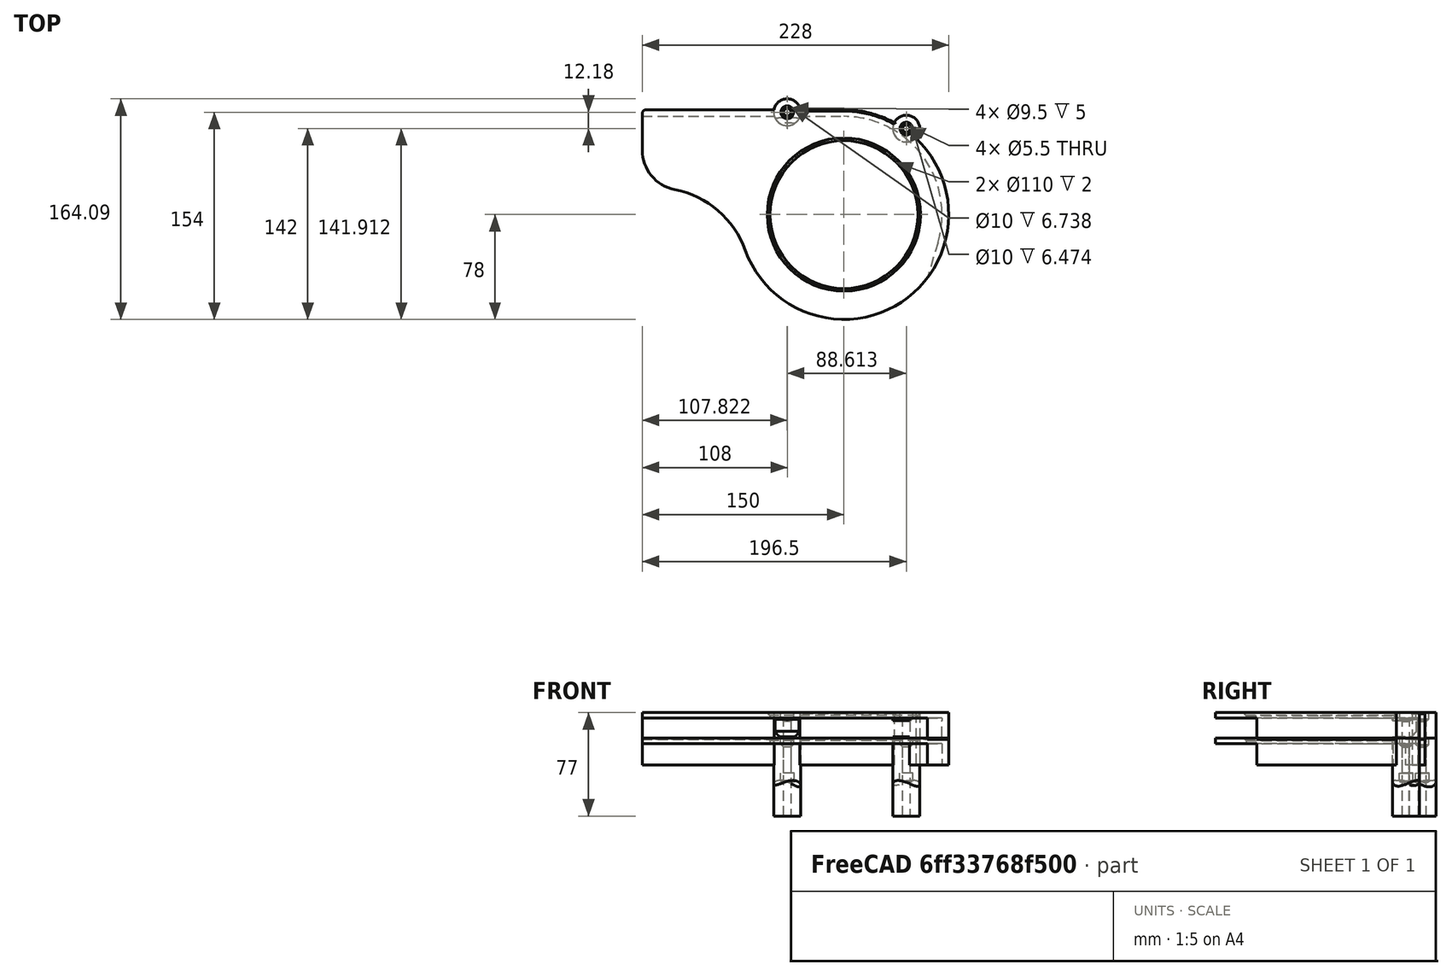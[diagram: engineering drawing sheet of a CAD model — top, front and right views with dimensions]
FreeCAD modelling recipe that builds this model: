
FCSTD DOCUMENT  (FreeCAD 0.19R)
Label: R3
License: All rights reserved
LicenseURL: http://en.wikipedia.org/wiki/All_rights_reserved
objects: Part::Cylinder×6, Sketcher::SketchObject×5, Part::Cut×4, PartDesign::Pocket×3, PartDesign::Chamfer×3, PartDesign::Pad×2, Part::MultiFuse×2, PartDesign::Fillet×1, PartDesign::Body×1, Part::Chamfer×1
note: 37 computed .brp shape members not serialized (recipe doc carries the construction recipe); baked Part::Feature solids carry a one-line shape summary decoded from their .brp

FEATURE [Sketcher::SketchObject] Sketch
  FullyConstrained = true
  MapMode = 5
  Support = -> [XY_Plane]
  sketch-geometry (10):
    g0: LineSegment StartX=0 StartY=0 StartZ=0 EndX=121.094 EndY=169.768 EndZ=0
    g1: LineSegment StartX=-81.2548 StartY=143.617 StartZ=0 EndX=0 EndY=0 EndZ=0
    g2: Circle CenterX=0 CenterY=0 CenterZ=0 NormalX=0 NormalY=0 NormalZ=1 AngleXU=0 Radius=73
    g3: LineSegment StartX=-228.06 StartY=73 StartZ=0 EndX=0 EndY=73 EndZ=0
    g4: LineSegment StartX=2.39e-14 StartY=78 StartZ=0 EndX=-150 EndY=78 EndZ=0
    g5: ArcOfCircle CenterX=0 CenterY=0 CenterZ=0 NormalX=0 NormalY=0 NormalZ=1 AngleXU=0 Radius=78 StartAngle=3.48916 EndAngle=7.85398
    g6: LineSegment StartX=-150 StartY=78 StartZ=0 EndX=-150 EndY=48 EndZ=0
    g7: ArcOfCircle CenterX=-120 CenterY=48 CenterZ=0 NormalX=0 NormalY=0 NormalZ=1 AngleXU=0 Radius=30 StartAngle=3.14159 EndAngle=4.51567
    g8: ArcOfCircle CenterX=-139.648 CenterY=-50.5912 CenterZ=0 NormalX=0 NormalY=0 NormalZ=1 AngleXU=0 Radius=70.53 StartAngle=0.347568 EndAngle=1.37408
    g9: Circle CenterX=0 CenterY=0 CenterZ=0 NormalX=0 NormalY=0 NormalZ=1 AngleXU=0 Radius=55
  constraints (28):
    c: Coincident(g0,g-1)
    c: Coincident(g1,g-1)
    c: Angle(g1) = -1.05592
    c: Angle(g0,g1) = 1.13446
    c: Coincident(g2,g-1)
    c: Radius(g2) = 73
    c: Tangent(g3,g2)
    c: Angle(g3) = 0
    c: PointOnObject(g4,g-2)
    c: Coincident(g5,g-1)
    c: Coincident(g5,g4)
    c: Radius(g5) = 78
    c: Coincident(g6,g4)
    c: Vertical(g6)
    c: Tangent(g5,g8) = 1.5708
    c: Tangent(g8,g7) = 1.5708
    c: Tangent(g7,g6) = -1.5708
    c: Distance(g4) = 150
    c: Radius(g7) = 30
    c: Radius(g8) = 70.53
    c: Horizontal(g4)
    c: Distance(g6) = 30
    c: Distance(g0) = 208.53
    c: Distance(g1) = 165.01
    c: Distance(g3) = 228.06
    c: PointOnObject(g3,g-2)
    c: Coincident(g9,g5)
    c: Radius(g9) = 55
FEATURE [PartDesign::Pad] Pad
  Direction = (1,1,1)
  Length = 20
  Length2 = 100
  Profile = -> Sketch
  Type = 0
FEATURE [Sketcher::SketchObject] Sketch001
  FullyConstrained = true
  MapMode = 5
  Placement = pos=(0,0,0) rot=(1,0,0;3.14159rad)
  Support = -> [Pad]
  sketch-geometry (4):
    g0: LineSegment StartX=-300 StartY=-73 StartZ=0 EndX=0 EndY=-73 EndZ=0
    g1: ArcOfCircle CenterX=0 CenterY=0 CenterZ=0 NormalX=0 NormalY=0 NormalZ=1 AngleXU=0 Radius=73 StartAngle=4.71239 EndAngle=6.57087
    g2: LineSegment StartX=70 StartY=20.7123 StartZ=0 EndX=34.9593 EndY=139.137 EndZ=0
    g3: LineSegment StartX=34.9593 StartY=139.137 StartZ=0 EndX=-300 EndY=-73 EndZ=0
  constraints (11):
    c: PointOnObject(g0,g-2)
    c: Horizontal(g0)
    c: Coincident(g1,g-1)
    c: Coincident(g1,g0)
    c: DistanceX(g1) = 70
    c: Radius(g1) = 73
    c: Tangent(g1,g2) = -1.5708
    c: Coincident(g2,g3)
    c: Coincident(g3,g0)
    c: Distance(g2) = 123.5
    c: Distance(g0) = 300
FEATURE [PartDesign::Pocket] Pocket
  BaseFeature = -> Pad
  Length = 16
  Length2 = 100
  Profile = -> Sketch001
  Type = 0
FEATURE [Sketcher::SketchObject] Sketch002
  FullyConstrained = true
  MapMode = 5
  Placement = pos=(0,0,20) rot=(0,0,1;0rad)
  Support = -> [Pocket]
  sketch-geometry (4):
    g0: LineSegment StartX=-72.7214 StartY=131.193 StartZ=0 EndX=0 EndY=0 EndZ=0
    g1: LineSegment StartX=0 StartY=0 StartZ=0 EndX=88.1678 EndY=121.353 EndZ=0
    g2: Circle CenterX=-42.1784 CenterY=76.0919 CenterZ=0 NormalX=0 NormalY=0 NormalZ=1 AngleXU=0 Radius=10
    g3: Circle CenterX=46.435 CenterY=63.9123 CenterZ=0 NormalX=0 NormalY=0 NormalZ=1 AngleXU=0 Radius=10
  constraints (12):
    c: Coincident(g0,g-1)
    c: Angle(g0) = -1.06465
    c: Coincident(g1,g-1)
    c: Angle(g1,g0) = 1.13446
    c: Distance(g1) = 150
    c: Distance(g0) = 150
    c: Diameter(g3) = 20
    c: Equal(g3,g2)
    c: PointOnObject(g2,g0)
    c: PointOnObject(g3,g1)
    c: Distance(g-1,g3) = 79
    c: Distance(g-1,g2) = 87
FEATURE [PartDesign::Pad] Pad001
  BaseFeature = -> Pocket
  Direction = (1,1,1)
  Length = 58
  Length2 = 100
  Profile = -> Sketch002
  Reversed = true
  Type = 0
FEATURE [Sketcher::SketchObject] Sketch003
  ExternalGeometry = -> [Pad001]
  FullyConstrained = true
  MapMode = 5
  Placement = pos=(0,0,20) rot=(0,0,1;0rad)
  Support = -> [Pad001]
  sketch-geometry (2):
    g0: Circle CenterX=-42.1784 CenterY=76.0919 CenterZ=0 NormalX=0 NormalY=0 NormalZ=1 AngleXU=0 Radius=2.75
    g1: Circle CenterX=46.435 CenterY=63.9123 CenterZ=0 NormalX=0 NormalY=0 NormalZ=1 AngleXU=0 Radius=2.75
  constraints (4):
    c: Diameter(g0) = 5.5
    c: Equal(g0,g1)
    c: Coincident(g0,g-3)
    c: Coincident(g1,g-4)
FEATURE [PartDesign::Pocket] Pocket001
  BaseFeature = -> Pad001
  Length = 5
  Length2 = 100
  Profile = -> Sketch003
  Type = 1
FEATURE [Sketcher::SketchObject] Sketch004
  ExternalGeometry = -> [Pocket001]
  FullyConstrained = true
  MapMode = 5
  Placement = pos=(0,0,20) rot=(0,0,1;0rad)
  Support = -> [Pocket001]
  sketch-geometry (2):
    g0: Circle CenterX=46.435 CenterY=63.9123 CenterZ=0 NormalX=0 NormalY=0 NormalZ=1 AngleXU=0 Radius=4.75
    g1: Circle CenterX=-42.1784 CenterY=76.0919 CenterZ=0 NormalX=0 NormalY=0 NormalZ=1 AngleXU=0 Radius=4.75
  constraints (4):
    c: Diameter(g1) = 9.5
    c: Coincident(g1,g-4)
    c: Coincident(g0,g-5)
    c: Diameter(g0) = 9.5
FEATURE [PartDesign::Pocket] Pocket002
  BaseFeature = -> Pocket001
  Length = 5
  Length2 = 100
  Profile = -> Sketch004
  Type = 0
FEATURE [Part::Cylinder] Cylinder
  Angle = 360
  AttacherType = Attacher::AttachEngine3D
  Height = 100
  Placement = pos=(0,0,-45) rot=(-0.810679,0.585491,0;1.5708rad)
  Radius = 14.5
FEATURE [Part::Cylinder] Cylinder001
  Angle = 360
  AttacherType = Attacher::AttachEngine3D
  Height = 100
  Placement = pos=(0,0,-45) rot=(-0.8704,-0.492345,0;1.5708rad)
  Radius = 14.5
FEATURE [Part::Cylinder] Cylinder002
  Angle = 360
  AttacherType = Attacher::AttachEngine3D
  Height = 10
  Placement = pos=(-42,76,-35) rot=(0,0,1;0rad)
  Radius = 5
FEATURE [Part::Cylinder] Cylinder003
  Angle = 360
  AttacherType = Attacher::AttachEngine3D
  Height = 10
  Placement = pos=(46.5,64,-35) rot=(0,0,1;0rad)
  Radius = 5
FEATURE [Part::MultiFuse] Fusion
  Shapes = -> [Cylinder,Cylinder001]
FEATURE [Part::MultiFuse] Fusion001
  Shapes = -> [Cylinder003,Cylinder002]
FEATURE [PartDesign::Chamfer] Chamfer
  Angle = 45
  Base = -> Pocket002 [Edge82,Edge78]
  BaseFeature = -> Pocket002
  ChamferType = 0
  FlipDirection = false
  Size = 1.6
  Size2 = 1
  SupportTransform = false
FEATURE [PartDesign::Chamfer] Chamfer001
  Angle = 45
  Base = -> Chamfer [Edge66]
  BaseFeature = -> Chamfer
  ChamferType = 0
  FlipDirection = false
  Size = 2
  Size2 = 1
  SupportTransform = false
FEATURE [PartDesign::Chamfer] Chamfer002
  Angle = 45
  Base = -> Chamfer001 [Edge11]
  BaseFeature = -> Chamfer001
  ChamferType = 0
  FlipDirection = false
  Size = 1
  Size2 = 1
  SupportTransform = false
FEATURE [PartDesign::Fillet] Fillet
  Base = -> Chamfer002 [Edge38]
  BaseFeature = -> Chamfer002
  Radius = 3
  SupportTransform = false
FEATURE [PartDesign::Body] Body
  Group = -> [Sketch,Pad,Sketch001,Pocket,Sketch002,Pad001,Sketch003,Pocket001,Sketch004,Pocket002,Chamfer,Chamfer001,Chamfer002,Fillet]
  Origin = -> Origin
  Tip = -> Fillet
FEATURE [Part::Cut] Cut
  Base = -> Fillet
  Tool = -> Fusion
FEATURE [Part::Cut] Cut001
  Base = -> Cut
  Placement = pos=(0,0,19) rot=(0,0,1;0rad)
  Tool = -> Fusion001
FEATURE [Part::Cylinder] Cylinder004
  Angle = 360
  AttacherType = Attacher::AttachEngine3D
  Height = 12
  Placement = pos=(0,0,21) rot=(0,0,1;0rad)
  Radius = 73
FEATURE [Part::Cut] Cut002
  Base = -> Cut001
  Tool = -> Cylinder004
FEATURE [Part::Cylinder] Cylinder005
  Angle = 360
  AttacherType = Attacher::AttachEngine3D
  Height = 13
  Placement = pos=(-42,-14,21) rot=(0,0,1;0rad)
  Radius = 86
FEATURE [Part::Cut] Cut003
  Base = -> Cut002
  Tool = -> Cylinder005
FEATURE [Part::Chamfer] Chamfer003
  Base = -> Cut003
  Edges = 1 edges r=4: [Edge111]
